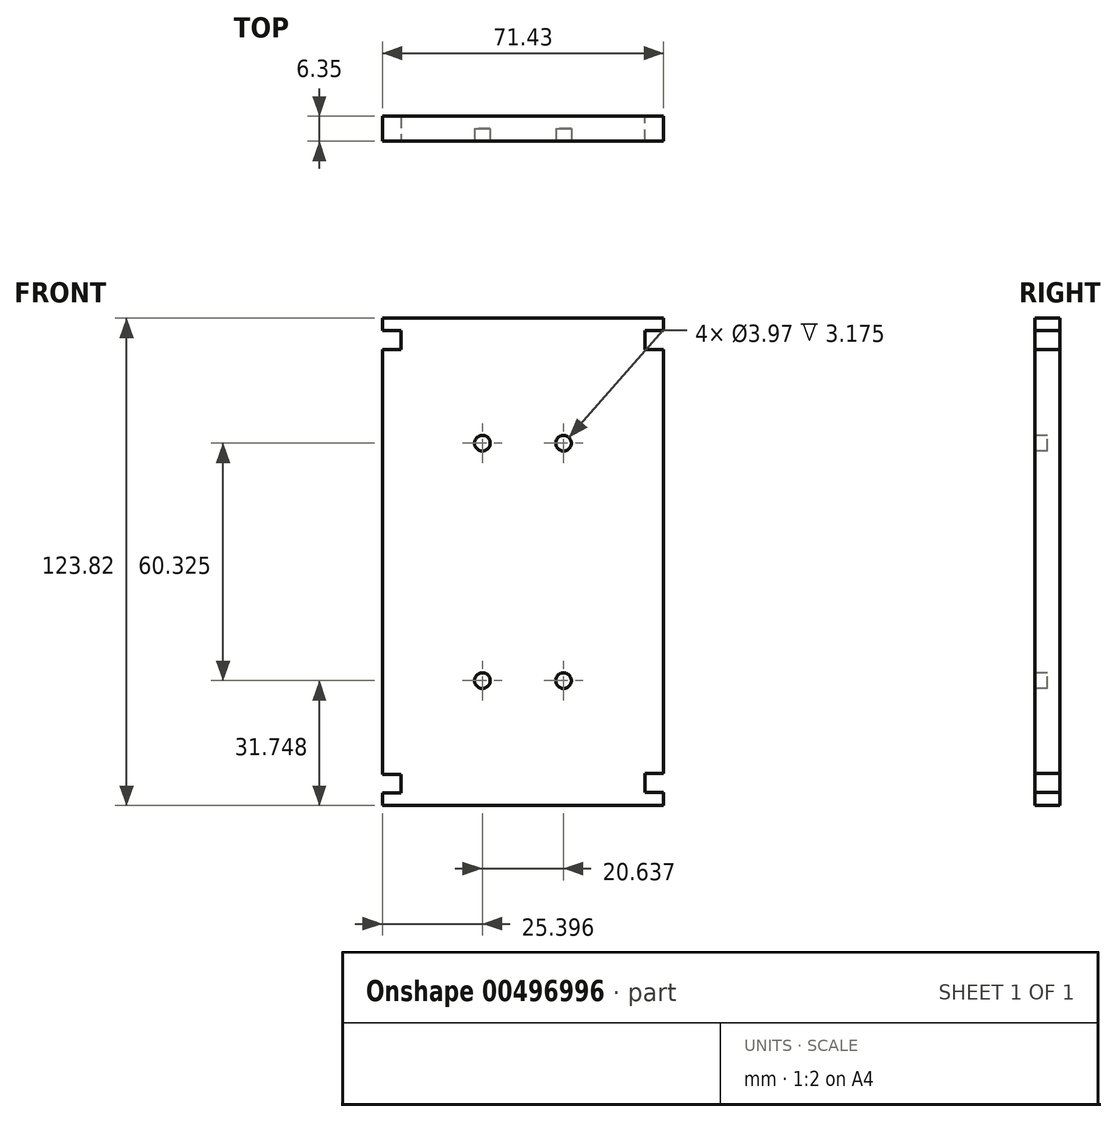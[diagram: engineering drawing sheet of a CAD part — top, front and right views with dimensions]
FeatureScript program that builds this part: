
annotation { "Feature Type Name" : "Feature", "Feature Type Description" : "" }
export const myFeature = defineFeature(function(context is Context, id is Id, definition is map)
    precondition{}
    {
        {
            var Q0;
            Q0=qCreatedBy(makeId("Front.planeOp"),FACE);
            var sketch = newSketch(context, id + "F0", { "sketchPlane" : qUnion([Q0])});
            skLineSegment(sketch, "E0.bottom", {"start": v(-34.11, 87.36) * mm, "end": v(37.32, 87.36) * mm});
            skLineSegment(sketch, "E0.top", {"start": v(-34.11, -36.46) * mm, "end": v(37.32, -36.46) * mm});
            skLineSegment(sketch, "E0.left", {"start": v(-34.11, 87.36) * mm, "end": v(-34.11, -36.46) * mm});
            skLineSegment(sketch, "E0.right", {"start": v(37.32, 87.36) * mm, "end": v(37.32, -36.46) * mm});
            skSolve(sketch);
        }
        {
            var Q0;
            Q0=makeQuery(id+"F0.imprint","IMPRINT",FACE,{"disambiguationData":[TD([[makeQuery(id+"F0.imprint","IMPRINT",EDGE,{"derivedFrom":sQuery(id+"F0.wireOp",EDGE,"E0.bottom")}),-1.0]])]});
            extrude(context, id + "F1", {"entities" : qUnion([Q0]), "depth" : 6.35 * mm});
        }
        {
            var Q0;
            Q0=makeQuery(id+"F1.opExtrude","SWEPT_FACE",FACE,{"disambiguationData":[OSD([sQuery(id+"F0.wireOp",EDGE,"E0.right")])]});
            var sketch = newSketch(context, id + "F2", { "sketchPlane" : qUnion([Q0])});
            skLineSegment(sketch, "E1.bottom", {"start": v(-6.35, 84.19) * mm, "end": v(0, 84.19) * mm});
            skLineSegment(sketch, "E1.top", {"start": v(-6.35, 79.43) * mm, "end": v(0, 79.43) * mm});
            skLineSegment(sketch, "E1.left", {"start": v(-6.35, 84.19) * mm, "end": v(-6.35, 79.43) * mm});
            skLineSegment(sketch, "E1.right", {"start": v(0, 84.19) * mm, "end": v(0, 79.43) * mm});
            skLineSegment(sketch, "E2", {"start": v(-6.35, 87.36) * mm, "end": v(0, 87.36) * mm});
            skSolve(sketch);
        }
        {
            var Q0;
            Q0=makeQuery(id+"F2.imprint","IMPRINT",FACE,{"disambiguationData":[TD([[makeQuery(id+"F2.imprint","IMPRINT",EDGE,{"derivedFrom":sQuery(id+"F2.wireOp",EDGE,"E1.bottom")}),-1.0]])]});
            extrude(context, id + "F3", {"entities" : qUnion([Q0]), "operationType" : NewBodyOperationType.REMOVE, "oppositeDirection" : true, "depth" : 4.76 * mm});
        }
        {
            var Q0;
            Q0=makeQuery(id+"F1.opExtrude","SWEPT_FACE",FACE,{"disambiguationData":[OSD([sQuery(id+"F0.wireOp",EDGE,"E0.right")])]});
            var sketch = newSketch(context, id + "F4", { "sketchPlane" : qUnion([Q0])});
            skLineSegment(sketch, "E3.bottom", {"start": v(-6.35, -28.32) * mm, "end": v(0, -28.32) * mm});
            skLineSegment(sketch, "E3.top", {"start": v(-6.35, -33.08) * mm, "end": v(0, -33.08) * mm});
            skLineSegment(sketch, "E3.left", {"start": v(-6.35, -28.32) * mm, "end": v(-6.35, -33.08) * mm});
            skLineSegment(sketch, "E3.right", {"start": v(0, -28.32) * mm, "end": v(0, -33.08) * mm});
            skLineSegment(sketch, "E4", {"start": v(0, -36.26) * mm, "end": v(-6.3, -36.26) * mm});
            skSolve(sketch);
        }
        {
            var Q0;
            Q0=makeQuery(id+"F4.imprint","IMPRINT",FACE,{"disambiguationData":[TD([[makeQuery(id+"F4.imprint","IMPRINT",EDGE,{"derivedFrom":sQuery(id+"F4.wireOp",EDGE,"E3.bottom")}),-1.0]])]});
            extrude(context, id + "F5", {"entities" : qUnion([Q0]), "operationType" : NewBodyOperationType.REMOVE, "oppositeDirection" : true, "depth" : 4.76 * mm});
        }
        {
            var Q0;
            Q0=makeQuery(id+"F1.opExtrude","SWEPT_FACE",FACE,{"disambiguationData":[OSD([sQuery(id+"F0.wireOp",EDGE,"E0.left")])]});
            var sketch = newSketch(context, id + "F6", { "sketchPlane" : qUnion([Q0])});
            skLineSegment(sketch, "E5.bottom", {"start": v(0, 84.19) * mm, "end": v(6.35, 84.19) * mm});
            skLineSegment(sketch, "E5.top", {"start": v(0, 79.43) * mm, "end": v(6.35, 79.43) * mm});
            skLineSegment(sketch, "E5.left", {"start": v(0, 84.19) * mm, "end": v(0, 79.43) * mm});
            skLineSegment(sketch, "E5.right", {"start": v(6.35, 84.19) * mm, "end": v(6.35, 79.43) * mm});
            skLineSegment(sketch, "E6", {"start": v(0, 87.36) * mm, "end": v(6.35, 87.36) * mm});
            skSolve(sketch);
        }
        {
            var Q0;
            Q0=makeQuery(id+"F6.imprint","IMPRINT",FACE,{"disambiguationData":[TD([[makeQuery(id+"F6.imprint","IMPRINT",EDGE,{"derivedFrom":sQuery(id+"F6.wireOp",EDGE,"E5.bottom")}),-1.0]])]});
            extrude(context, id + "F7", {"entities" : qUnion([Q0]), "operationType" : NewBodyOperationType.REMOVE, "oppositeDirection" : true, "depth" : 4.76 * mm});
        }
        {
            var Q0;
            {var subQ1=sQuery(id+"F0.wireOp",EDGE,"E0.left");var subQ2=sQuery(id+"F0.wireOp",EDGE,"E0.top");Q0=makeQuery(id+"F7.boolean.opBoolean","SPLIT",FACE,{"disambiguationData":[TD([makeQuery(id+"F1.opExtrude","SWEPT_FACE",FACE,{"disambiguationData":[OSD([subQ2])]})])],"derivedFrom":makeQuery(id+"F1.opExtrude","SWEPT_FACE",FACE,{"disambiguationData":[OSD([subQ1])]})});}
            var sketch = newSketch(context, id + "F8", { "sketchPlane" : qUnion([Q0])});
            skLineSegment(sketch, "E7.bottom", {"start": v(0, -28.52) * mm, "end": v(6.35, -28.52) * mm});
            skLineSegment(sketch, "E7.top", {"start": v(0, -33.29) * mm, "end": v(6.35, -33.29) * mm});
            skLineSegment(sketch, "E7.left", {"start": v(0, -28.52) * mm, "end": v(0, -33.29) * mm});
            skLineSegment(sketch, "E7.right", {"start": v(6.35, -28.52) * mm, "end": v(6.35, -33.29) * mm});
            skLineSegment(sketch, "E8", {"start": v(0, -36.46) * mm, "end": v(6.35, -36.46) * mm});
            skSolve(sketch);
        }
        {
            var Q0;
            Q0=makeQuery(id+"F8.imprint","IMPRINT",FACE,{"disambiguationData":[TD([[makeQuery(id+"F8.imprint","IMPRINT",EDGE,{"derivedFrom":sQuery(id+"F8.wireOp",EDGE,"E7.bottom")}),-1.0]])]});
            extrude(context, id + "F9", {"entities" : qUnion([Q0]), "operationType" : NewBodyOperationType.REMOVE, "oppositeDirection" : true, "depth" : 4.76 * mm});
        }
        {
            var Q0;
            Q0=makeQuery(id+"F1.opExtrude","CAP_FACE",FACE,{"disambiguationData":[OSD([sQuery(id+"F0.wireOp",EDGE,"E0.bottom"),sQuery(id+"F0.wireOp",EDGE,"E0.top"),sQuery(id+"F0.wireOp",EDGE,"E0.left"),sQuery(id+"F0.wireOp",EDGE,"E0.right")])],"isStart":false});
            var sketch = newSketch(context, id + "F10", { "sketchPlane" : qUnion([Q0])});
            skCircle(sketch, "E9", {"center": v(-8.71, 55.61) * mm, "radius": 1.98 * mm});
            skCircle(sketch, "E10", {"center": v(11.92, 55.61) * mm, "radius": 1.98 * mm});
            skCircle(sketch, "E11", {"center": v(-8.71, -4.71) * mm, "radius": 1.98 * mm});
            skCircle(sketch, "E12", {"center": v(11.92, -4.71) * mm, "radius": 1.98 * mm});
            skSolve(sketch);
        }
        {
            var Q0;
            Q0=makeQuery(id+"F10.imprint","IMPRINT",FACE,{"disambiguationData":[TD([[makeQuery(id+"F10.imprint","IMPRINT",EDGE,{"derivedFrom":sQuery(id+"F10.wireOp",EDGE,"E9")}),1.0]])]});
            var Q1;
            Q1=makeQuery(id+"F10.imprint","IMPRINT",FACE,{"disambiguationData":[TD([[makeQuery(id+"F10.imprint","IMPRINT",EDGE,{"derivedFrom":sQuery(id+"F10.wireOp",EDGE,"E10")}),1.0]])]});
            var Q2;
            Q2=makeQuery(id+"F10.imprint","IMPRINT",FACE,{"disambiguationData":[TD([[makeQuery(id+"F10.imprint","IMPRINT",EDGE,{"derivedFrom":sQuery(id+"F10.wireOp",EDGE,"E11")}),1.0]])]});
            var Q3;
            Q3=makeQuery(id+"F10.imprint","IMPRINT",FACE,{"disambiguationData":[TD([[makeQuery(id+"F10.imprint","IMPRINT",EDGE,{"derivedFrom":sQuery(id+"F10.wireOp",EDGE,"E12")}),1.0]])]});
            extrude(context, id + "F11", {"entities" : qUnion([Q0, Q1, Q2, Q3]), "operationType" : NewBodyOperationType.REMOVE, "oppositeDirection" : true, "depth" : 3.17 * mm});
        }
    });
